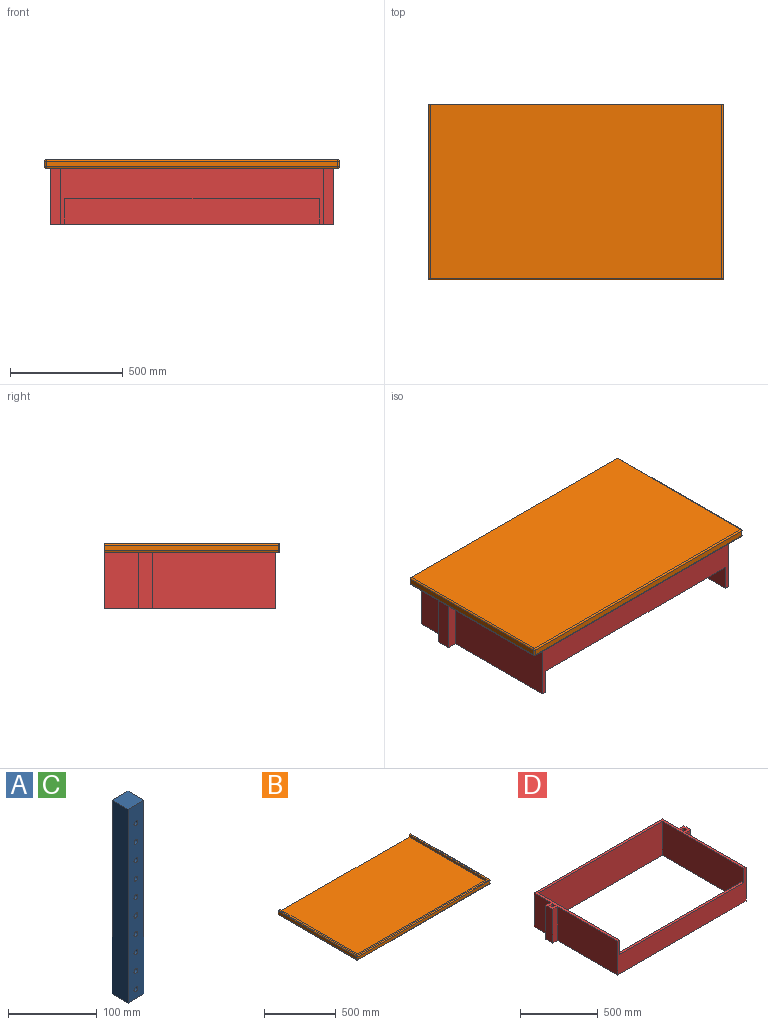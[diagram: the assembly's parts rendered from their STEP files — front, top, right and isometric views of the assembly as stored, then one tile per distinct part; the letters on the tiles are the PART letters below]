
ASSEMBLY  parts=4 mates=3
PART A: 16 faces, bbox 25.4x25.4x266.7 mm
  f0: plane 266.7x25.4mm, normal (-1,0,0), area 6774.2mm2, adj f1,f13,f14,f15
  f1: plane 25.4x25.4mm, normal (0,0,-1), area 645.2mm2, adj f0,f2,f14,f15
  f2: plane 266.7x25.4mm, normal (1,0,0), area 6774.2mm2, adj f1,f13,f14,f15
  f3: cylinder r=3.17mm len=25.4mm, axis (0,1,0), area 506.7mm2, adj f14,f15
  f4: cylinder r=3.17mm len=25.4mm, axis (0,1,0), area 506.7mm2, adj f14,f15
  f5: cylinder r=3.17mm len=25.4mm, axis (0,1,0), area 506.7mm2, adj f14,f15
  f6: cylinder r=3.17mm len=25.4mm, axis (0,1,0), area 506.7mm2, adj f14,f15
  f7: cylinder r=3.17mm len=25.4mm, axis (0,1,0), area 506.7mm2, adj f14,f15
  f8: cylinder r=3.17mm len=25.4mm, axis (0,1,0), area 506.7mm2, adj f14,f15
  f9: cylinder r=3.17mm len=25.4mm, axis (0,1,0), area 506.7mm2, adj f14,f15
  f10: cylinder r=3.17mm len=25.4mm, axis (0,1,0), area 506.7mm2, adj f14,f15
  f11: cylinder r=3.17mm len=25.4mm, axis (0,1,0), area 506.7mm2, adj f14,f15
  f12: cylinder r=3.17mm len=25.4mm, axis (0,1,0), area 506.7mm2, adj f14,f15
  f13: plane 25.4x25.4mm, normal (0,0,1), area 645.2mm2, adj f0,f2,f14,f15
  f14: plane 266.7x25.4mm, normal (0,-1,0), area 6457.5mm2, adj f0,f1,f2,f3,f4,f5,f6,f7
  f15: plane 266.7x25.4mm, normal (0,1,0), area 6457.5mm2, adj f0,f1,f2,f3,f4,f5,f6,f7
PART B: 22 faces, bbox 1308.1x781.1x38.1 mm
  f0: plane 1308.1x38.1mm, normal (0,1,0), area 25610.5mm2, adj f1,f2,f3,f5,f7,f8,f9,f10
  f1: plane 1270x762mm, normal (0,0,1), area 967740mm2, adj f0,f3,f4,f5
  f2: plane 1295.4x774.7mm, normal (0,0,-1), area 1003546.4mm2, adj f0,f12,f17,f18
  f3: plane 762x19.05mm, normal (1,0,0), area 14516.1mm2, adj f0,f1,f4,f9
  f4: plane 1270x19.05mm, normal (0,1,0), area 24193.5mm2, adj f1,f3,f5,f9
  f5: plane 762x19.05mm, normal (-1,0,0), area 14516.1mm2, adj f0,f1,f4,f9
  f6: plane 1295.4x25.4mm, normal (0,-1,0), area 32903.2mm2, adj f11,f16,f17,f21
  f7: plane 774.7x25.4mm, normal (1,0,0), area 19677.4mm2, adj f0,f10,f11,f12
  f8: plane 774.7x25.4mm, normal (-1,0,0), area 19677.4mm2, adj f0,f15,f18,f21
  f9: plane 1295.4x774.7mm, normal (0,0,1), area 35806.4mm2, adj f0,f3,f4,f5,f10,f15,f16
  f10: cylinder r=6.35mm len=774.7mm, axis (0,-1,0), area 7727.3mm2, adj f0,f7,f9,f13
  f11: cylinder r=6.35mm len=25.4mm, axis (0,0,-1), area 253.4mm2, adj f6,f7,f13,f14
  f12: cylinder r=6.35mm len=774.7mm, axis (0,1,0), area 7727.3mm2, adj f0,f2,f7,f14
  f13: sphere r=6.35mm, area 63.3mm2, adj f10,f11,f16
  f14: sphere r=6.35mm, area 63.3mm2, adj f11,f12,f17
  f15: cylinder r=6.35mm len=774.7mm, axis (0,1,0), area 7727.3mm2, adj f0,f8,f9,f19
  f16: cylinder r=6.35mm len=1295.4mm, axis (-1,0,0), area 12921mm2, adj f6,f9,f13,f19
  f17: cylinder r=6.35mm len=1295.4mm, axis (1,0,0), area 12921mm2, adj f2,f6,f14,f20
  f18: cylinder r=6.35mm len=774.7mm, axis (0,-1,0), area 7727.3mm2, adj f0,f2,f8,f20
  f19: sphere r=6.35mm, area 63.3mm2, adj f15,f16,f21
  f20: sphere r=6.35mm, area 63.3mm2, adj f17,f18,f21
  f21: cylinder r=6.35mm len=25.4mm, axis (0,0,1), area 253.4mm2, adj f6,f8,f19,f20
PART C: same geometry as A
PART D: 27 faces, bbox 1257.3x762x266.7 mm
  f0: plane 266.7x25.4mm, normal (1,0,0), area 6774.2mm2, adj f11,f12,f22,f24
  f1: plane 547.58x266.7mm, normal (1,0,0), area 146040.7mm2, adj f9,f11,f12,f25
  f2: plane 266.7x25.4mm, normal (-1,0,0), area 6774.2mm2, adj f11,f12,f18,f20
  f3: plane 547.58x266.7mm, normal (-1,0,0), area 146040.7mm2, adj f9,f11,f12,f17
  f4: plane 742.95x266.7mm, normal (-1,0,0), area 195241.5mm2, adj f5,f9,f11,f12,f13,f14
  f5: plane 1130.3x266.7mm, normal (0,-1,0), area 301451mm2, adj f4,f10,f11,f12
  f6: plane 266.7x150.92mm, normal (1,0,0), area 40249.2mm2, adj f7,f11,f12,f21
  f7: plane 1168.4x266.7mm, normal (0,1,0), area 311612.3mm2, adj f6,f8,f11,f12
  f8: plane 266.7x150.92mm, normal (-1,0,0), area 40249.2mm2, adj f7,f11,f12,f15
  f9: plane 1168.4x266.7mm, normal (0,-1,0), area 182419mm2, adj f1,f3,f4,f10,f11,f12,f14
  f10: plane 742.95x266.7mm, normal (1,0,0), area 195241.5mm2, adj f5,f9,f11,f12,f13,f14
  f11: plane 1257.3x762mm, normal (0,0,1), area 54919.2mm2, adj f0,f1,f2,f3,f4,f5,f6,f7
  f12: plane 1257.3x762mm, normal (0,0,-1), area 76451.5mm2, adj f0,f1,f2,f3,f4,f5,f6,f7
  f13: plane 1130.3x152.4mm, normal (0,1,0), area 172257.7mm2, adj f4,f10,f12,f14
  f14: plane 1130.3x19.05mm, normal (0,0,1), area 21532.2mm2, adj f4,f9,f10,f13
  f15: plane 266.7x44.45mm, normal (0,1,0), area 11854.8mm2, adj f8,f11,f12,f16
  f16: plane 266.7x63.5mm, normal (-1,0,0), area 16935.5mm2, adj f11,f12,f15,f17
  f17: plane 266.7x44.45mm, normal (0,-1,0), area 11854.8mm2, adj f3,f11,f12,f16
  f18: plane 266.7x25.4mm, normal (0,1,0), area 6774.2mm2, adj f2,f11,f12,f19
  f19: plane 266.7x25.4mm, normal (1,0,0), area 6774.2mm2, adj f11,f12,f18,f20
  f20: plane 266.7x25.4mm, normal (0,-1,0), area 6774.2mm2, adj f2,f11,f12,f19
  f21: plane 266.7x44.45mm, normal (0,1,0), area 11854.8mm2, adj f6,f11,f12,f26
  f22: plane 266.7x25.4mm, normal (0,-1,0), area 6774.2mm2, adj f0,f11,f12,f23
  f23: plane 266.7x25.4mm, normal (-1,0,0), area 6774.2mm2, adj f11,f12,f22,f24
  f24: plane 266.7x25.4mm, normal (0,1,0), area 6774.2mm2, adj f0,f11,f12,f23
  f25: plane 266.7x44.45mm, normal (0,-1,0), area 11854.8mm2, adj f1,f11,f12,f26
  f26: plane 266.7x63.5mm, normal (1,0,0), area 16935.5mm2, adj f11,f12,f21,f25
PLACE A rot(axis=(0,0,-1),90deg) t=(-628.48,310.95,-135.01)mm
PLACE B rot(axis=(0,-1,0),180deg) t=(-98.34,39.18,109.78)mm
PLACE C rot(axis=(0,0,-1),90deg) t=(565.32,310.95,-135.01)mm
PLACE D rot(axis=(0,-1,0),180deg) t=(-170.8,5.59,90.73)mm
MATE slider A.f1 <-> D.f11  axis (0,0,-1) through (-653.88,322.9,-175.97)mm
MATE slider B.f1 <-> D.f12  axis (0,0,-1) through (-44.28,504.82,90.73)mm
MATE slider C.f1 <-> D.f11  axis (0,0,-1) through (565.32,322.9,-175.97)mm
